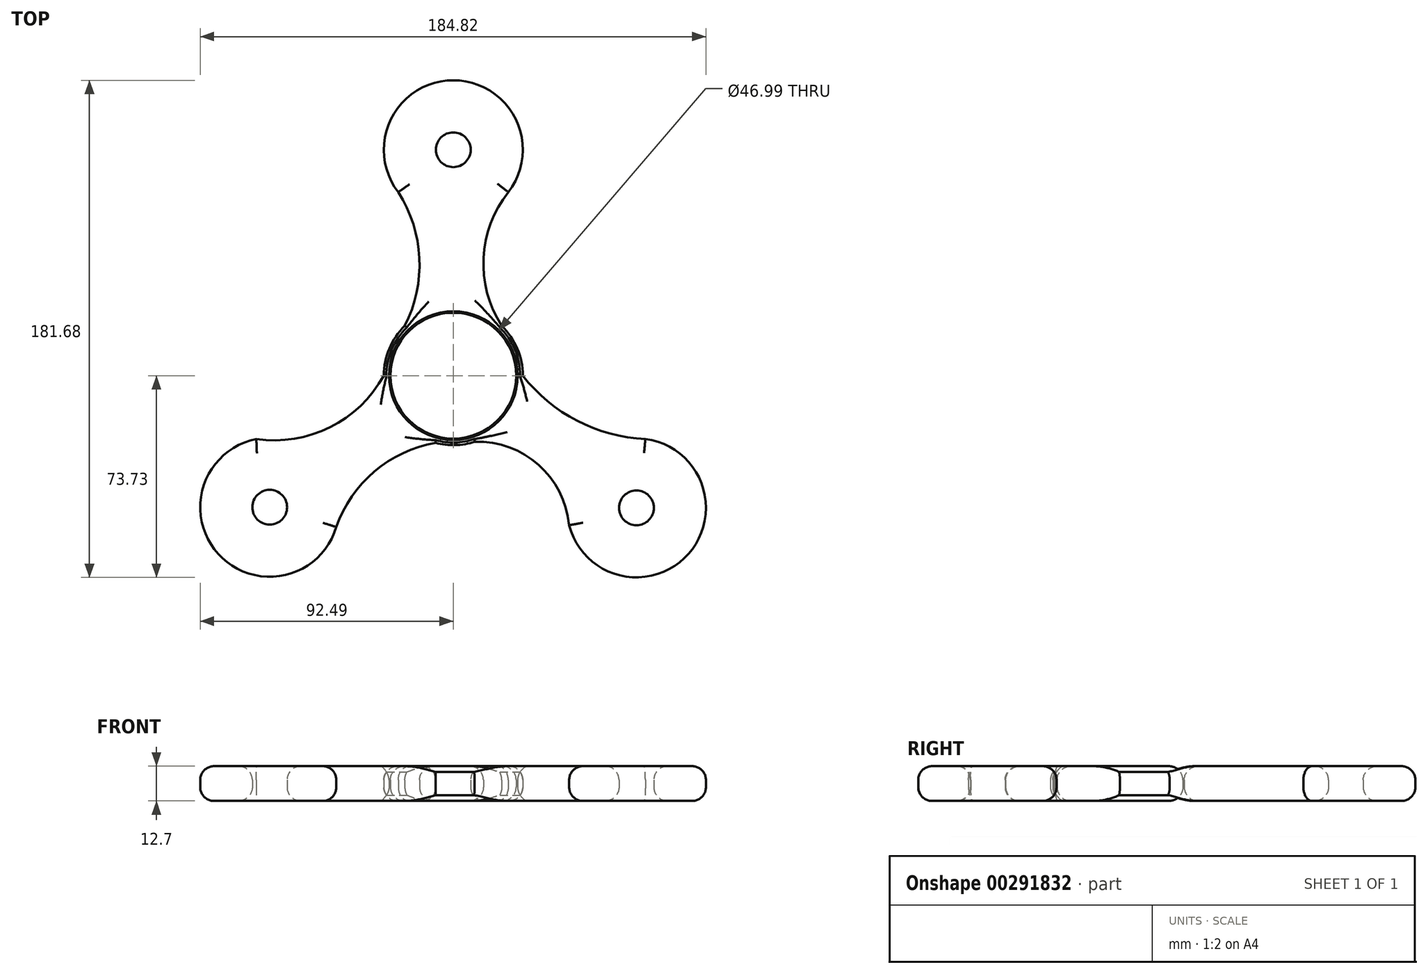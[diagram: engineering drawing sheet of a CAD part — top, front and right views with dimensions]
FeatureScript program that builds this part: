
annotation { "Feature Type Name" : "Feature", "Feature Type Description" : "" }
export const myFeature = defineFeature(function(context is Context, id is Id, definition is map)
    precondition{}
    {
        {
            var Q0;
            Q0=qCreatedBy(makeId("Top.planeOp"),FACE);
            var sketch = newSketch(context, id + "F0", { "sketchPlane" : qUnion([Q0])});
            skCircle(sketch, "E0", {"center": v(0, 0) * mm, "radius": 25.4 * mm});
            skCircle(sketch, "E1", {"center": v(0, 82.55) * mm, "radius": 25.4 * mm});
            skCircle(sketch, "E2", {"center": v(-67.09, -48.1) * mm, "radius": 25.4 * mm});
            skCircle(sketch, "E3", {"center": v(66.93, -48.33) * mm, "radius": 25.4 * mm});
            skArc(sketch, "E4", {"start": v(-71.96, -23.17) * mm, "mid": v(-45.05, -18.89) * mm, "end": v(-25.4, 0) * mm});
            skArc(sketch, "E5", {"start": v(-6.47, -24.56) * mm, "mid": v(-28.8, -35.02) * mm, "end": v(-42.74, -55.34) * mm});
            skArc(sketch, "E6", {"start": v(42.33, -54.66) * mm, "mid": v(31.12, -32.56) * mm, "end": v(7.8, -24.17) * mm});
            skArc(sketch, "E7", {"start": v(25.4, 0) * mm, "mid": v(45.25, -16.48) * mm, "end": v(70.19, -23.14) * mm});
            skArc(sketch, "E8", {"start": v(-17.72, 18.2) * mm, "mid": v(-12.4, 42.93) * mm, "end": v(-20.1, 67.03) * mm});
            skArc(sketch, "E9", {"start": v(20.1, 67.03) * mm, "mid": v(11.06, 43) * mm, "end": v(17.72, 18.2) * mm});
            skCircle(sketch, "E10", {"center": v(0, 82.55) * mm, "radius": 6.35 * mm});
            skCircle(sketch, "E11", {"center": v(-67.09, -48.1) * mm, "radius": 6.35 * mm});
            skCircle(sketch, "E12", {"center": v(66.93, -48.33) * mm, "radius": 6.35 * mm});
            skCircle(sketch, "E13", {"center": v(0, 0) * mm, "radius": 23.5 * mm});
            skSolve(sketch);
        }
        {
            var Q0;
            {var subQ0=sQuery(id+"F0.wireOp",EDGE,"E1");var subQ1=makeQuery(id+"F0.imprint","INTERSECT",VERTEX,{"derivedFrom":[subQ0,sQuery(id+"F0.wireOp",EDGE,"E8")]});Q0=makeQuery(id+"F0.imprint","IMPRINT",FACE,{"disambiguationData":[TD([[makeQuery(id+"F0.imprint","IMPRINT",EDGE,{"disambiguationData":[TD([[subQ1,-1.0]])],"derivedFrom":subQ0}),1.0]])]});}
            var Q1;
            {var subQ0=sQuery(id+"F0.wireOp",EDGE,"E8");Q1=makeQuery(id+"F0.imprint","IMPRINT",FACE,{"disambiguationData":[TD([[makeQuery(id+"F0.imprint","IMPRINT",EDGE,{"derivedFrom":subQ0}),-1.0]])]});}
            var Q2;
            {var subQ0=sQuery(id+"F0.wireOp",EDGE,"E0");var subQ5=makeQuery(id+"F0.imprint","INTERSECT",VERTEX,{"derivedFrom":[subQ0,sQuery(id+"F0.wireOp",EDGE,"E7")]});Q2=makeQuery(id+"F0.imprint","IMPRINT",FACE,{"disambiguationData":[TD([[makeQuery(id+"F0.imprint","IMPRINT",EDGE,{"disambiguationData":[TD([[subQ5,-1.0]])],"derivedFrom":subQ0}),1.0]])]});}
            var Q3;
            {var subQ3=sQuery(id+"F0.wireOp",EDGE,"E5");Q3=makeQuery(id+"F0.imprint","IMPRINT",FACE,{"disambiguationData":[TD([[makeQuery(id+"F0.imprint","IMPRINT",EDGE,{"derivedFrom":subQ3}),-1.0]])]});}
            var Q4;
            {var subQ0=sQuery(id+"F0.wireOp",EDGE,"E4");var subQ1=sQuery(id+"F0.wireOp",EDGE,"E2");var subQ2=makeQuery(id+"F0.imprint","INTERSECT",VERTEX,{"disambiguationData":[OD(0.0)],"derivedFrom":[subQ1,subQ0]});Q4=makeQuery(id+"F0.imprint","IMPRINT",FACE,{"disambiguationData":[TD([[makeQuery(id+"F0.imprint","IMPRINT",EDGE,{"disambiguationData":[TD([[subQ2,-1.0]])],"derivedFrom":subQ1}),1.0]])]});}
            var Q5;
            {var subQ0=sQuery(id+"F0.wireOp",EDGE,"E6");var subQ1=sQuery(id+"F0.wireOp",EDGE,"E0");var subQ2=makeQuery(id+"F0.imprint","INTERSECT",VERTEX,{"derivedFrom":[subQ1,subQ0]});Q5=makeQuery(id+"F0.imprint","IMPRINT",FACE,{"disambiguationData":[TD([[makeQuery(id+"F0.imprint","IMPRINT",EDGE,{"disambiguationData":[TD([[subQ2,-1.0]])],"derivedFrom":subQ1}),-1.0]])]});}
            var Q6;
            {var subQ0=sQuery(id+"F0.wireOp",EDGE,"E7");var subQ1=sQuery(id+"F0.wireOp",EDGE,"E3");var subQ2=makeQuery(id+"F0.imprint","INTERSECT",VERTEX,{"disambiguationData":[OD(1.0)],"derivedFrom":[subQ1,subQ0]});Q6=makeQuery(id+"F0.imprint","IMPRINT",FACE,{"disambiguationData":[TD([[makeQuery(id+"F0.imprint","IMPRINT",EDGE,{"disambiguationData":[TD([[subQ2,-1.0]])],"derivedFrom":subQ1}),1.0]])]});}
            var Q7;
            Q7=makeQuery(id+"F0.imprint","IMPRINT",FACE,{"disambiguationData":[TD([[makeQuery(id+"F0.imprint","IMPRINT",EDGE,{"derivedFrom":sQuery(id+"F0.wireOp",EDGE,"T1coXftw-NrjD-YKbX-frgJ-oNxXQp378vgS")}),1.0]])]});
            extrude(context, id + "F1", {"entities" : qUnion([Q0, Q1, Q2, Q3, Q4, Q5, Q6, Q7]), "depth" : 12.7 * mm, "offsetDistance" : 25.4 * mm});
        }
        {
            var Q0;
            {var subQ0=sQuery(id+"F0.wireOp",EDGE,"E0");Q0=makeQuery(id+"F1.opExtrude","CAP_EDGE",EDGE,{"disambiguationData":[OSD([subQ0]),TDD([makeQuery(id+"F0.imprint","IMPRINT",EDGE,{"disambiguationData":[TD([[makeQuery(id+"F0.imprint","INTERSECT",VERTEX,{"derivedFrom":[subQ0,sQuery(id+"F0.wireOp",EDGE,"E4")]}),1.0]])],"derivedFrom":subQ0})])],"isStart":false});}
            var Q1;
            {var subQ0=sQuery(id+"F0.wireOp",EDGE,"E0");Q1=makeQuery(id+"F1.opExtrude","CAP_EDGE",EDGE,{"disambiguationData":[OSD([subQ0]),TDD([makeQuery(id+"F0.imprint","IMPRINT",EDGE,{"disambiguationData":[TD([[makeQuery(id+"F0.imprint","INTERSECT",VERTEX,{"derivedFrom":[subQ0,sQuery(id+"F0.wireOp",EDGE,"E4")]}),1.0]])],"derivedFrom":subQ0})])],"isStart":true});}
            var Q2;
            Q2=makeQuery(id+"F1.opExtrude","CAP_EDGE",EDGE,{"disambiguationData":[OSD([sQuery(id+"F0.wireOp",EDGE,"E8")])],"isStart":true});
            var Q3;
            Q3=makeQuery(id+"F1.opExtrude","CAP_EDGE",EDGE,{"disambiguationData":[OSD([sQuery(id+"F0.wireOp",EDGE,"E8")])],"isStart":false});
            var Q4;
            Q4=makeQuery(id+"F1.opExtrude","CAP_EDGE",EDGE,{"disambiguationData":[OSD([sQuery(id+"F0.wireOp",EDGE,"E13")])],"isStart":false});
            var Q5;
            {var subQ0=sQuery(id+"F0.wireOp",EDGE,"E0");Q5=makeQuery(id+"F1.opExtrude","CAP_EDGE",EDGE,{"disambiguationData":[OSD([subQ0]),TDD([makeQuery(id+"F0.imprint","IMPRINT",EDGE,{"disambiguationData":[TD([[makeQuery(id+"F0.imprint","INTERSECT",VERTEX,{"derivedFrom":[subQ0,sQuery(id+"F0.wireOp",EDGE,"E7")]}),-1.0]])],"derivedFrom":subQ0})])],"isStart":false});}
            var Q6;
            {var subQ0=sQuery(id+"F0.wireOp",EDGE,"E0");Q6=makeQuery(id+"F1.opExtrude","CAP_EDGE",EDGE,{"disambiguationData":[OSD([subQ0]),TDD([makeQuery(id+"F0.imprint","IMPRINT",EDGE,{"disambiguationData":[TD([[makeQuery(id+"F0.imprint","INTERSECT",VERTEX,{"derivedFrom":[subQ0,sQuery(id+"F0.wireOp",EDGE,"E7")]}),-1.0]])],"derivedFrom":subQ0})])],"isStart":true});}
            var Q7;
            {var subQ0=sQuery(id+"F0.wireOp",EDGE,"E0");Q7=makeQuery(id+"F1.opExtrude","CAP_EDGE",EDGE,{"disambiguationData":[OSD([subQ0]),TDD([makeQuery(id+"F0.imprint","IMPRINT",EDGE,{"disambiguationData":[TD([[makeQuery(id+"F0.imprint","INTERSECT",VERTEX,{"derivedFrom":[subQ0,sQuery(id+"F0.wireOp",EDGE,"E5")]}),-1.0]])],"derivedFrom":subQ0})])],"isStart":true});}
            var Q8;
            Q8=makeQuery(id+"F1.opExtrude","CAP_EDGE",EDGE,{"disambiguationData":[OSD([sQuery(id+"F0.wireOp",EDGE,"E4")])],"isStart":true});
            var Q9;
            Q9=makeQuery(id+"F1.opExtrude","CAP_EDGE",EDGE,{"disambiguationData":[OSD([sQuery(id+"F0.wireOp",EDGE,"E5")])],"isStart":true});
            var Q10;
            Q10=makeQuery(id+"F1.opExtrude","CAP_EDGE",EDGE,{"disambiguationData":[OSD([sQuery(id+"F0.wireOp",EDGE,"E6")])],"isStart":true});
            var Q11;
            Q11=makeQuery(id+"F1.opExtrude","CAP_EDGE",EDGE,{"disambiguationData":[OSD([sQuery(id+"F0.wireOp",EDGE,"E6")])],"isStart":false});
            var Q12;
            Q12=makeQuery(id+"F1.opExtrude","CAP_EDGE",EDGE,{"disambiguationData":[OSD([sQuery(id+"F0.wireOp",EDGE,"E7")])],"isStart":true});
            var Q13;
            Q13=makeQuery(id+"F1.opExtrude","CAP_EDGE",EDGE,{"disambiguationData":[OSD([sQuery(id+"F0.wireOp",EDGE,"E7")])],"isStart":false});
            var Q14;
            Q14=makeQuery(id+"F1.opExtrude","CAP_EDGE",EDGE,{"disambiguationData":[OSD([sQuery(id+"F0.wireOp",EDGE,"E4")])],"isStart":false});
            var Q15;
            Q15=makeQuery(id+"F1.opExtrude","CAP_EDGE",EDGE,{"disambiguationData":[OSD([sQuery(id+"F0.wireOp",EDGE,"E5")])],"isStart":false});
            var Q16;
            Q16=makeQuery(id+"F1.opExtrude","CAP_EDGE",EDGE,{"disambiguationData":[OSD([sQuery(id+"F0.wireOp",EDGE,"E9")])],"isStart":false});
            var Q17;
            Q17=makeQuery(id+"F1.opExtrude","CAP_EDGE",EDGE,{"disambiguationData":[OSD([sQuery(id+"F0.wireOp",EDGE,"E3")])],"isStart":false});
            var Q18;
            Q18=makeQuery(id+"F1.opExtrude","CAP_EDGE",EDGE,{"disambiguationData":[OSD([sQuery(id+"F0.wireOp",EDGE,"E12")])],"isStart":false});
            var Q19;
            Q19=makeQuery(id+"F1.opExtrude","CAP_EDGE",EDGE,{"disambiguationData":[OSD([sQuery(id+"F0.wireOp",EDGE,"E12")])],"isStart":true});
            var Q20;
            Q20=makeQuery(id+"F1.opExtrude","CAP_EDGE",EDGE,{"disambiguationData":[OSD([sQuery(id+"F0.wireOp",EDGE,"E3")])],"isStart":true});
            var Q21;
            Q21=makeQuery(id+"F1.opExtrude","CAP_FACE",FACE,{"disambiguationData":[OSD([sQuery(id+"F0.wireOp",EDGE,"E0"),sQuery(id+"F0.wireOp",EDGE,"E1"),sQuery(id+"F0.wireOp",EDGE,"E2"),sQuery(id+"F0.wireOp",EDGE,"E3"),sQuery(id+"F0.wireOp",EDGE,"E4"),sQuery(id+"F0.wireOp",EDGE,"E5"),sQuery(id+"F0.wireOp",EDGE,"E6"),sQuery(id+"F0.wireOp",EDGE,"E7"),sQuery(id+"F0.wireOp",EDGE,"E8"),sQuery(id+"F0.wireOp",EDGE,"E9"),sQuery(id+"F0.wireOp",EDGE,"E10"),sQuery(id+"F0.wireOp",EDGE,"E11"),sQuery(id+"F0.wireOp",EDGE,"E12"),sQuery(id+"F0.wireOp",EDGE,"E13")])],"isStart":true});
            var Q22;
            Q22=makeQuery(id+"F1.opExtrude","CAP_FACE",FACE,{"disambiguationData":[OSD([sQuery(id+"F0.wireOp",EDGE,"E0"),sQuery(id+"F0.wireOp",EDGE,"E1"),sQuery(id+"F0.wireOp",EDGE,"E2"),sQuery(id+"F0.wireOp",EDGE,"E3"),sQuery(id+"F0.wireOp",EDGE,"E4"),sQuery(id+"F0.wireOp",EDGE,"E5"),sQuery(id+"F0.wireOp",EDGE,"E6"),sQuery(id+"F0.wireOp",EDGE,"E7"),sQuery(id+"F0.wireOp",EDGE,"E8"),sQuery(id+"F0.wireOp",EDGE,"E9"),sQuery(id+"F0.wireOp",EDGE,"E10"),sQuery(id+"F0.wireOp",EDGE,"E11"),sQuery(id+"F0.wireOp",EDGE,"E12"),sQuery(id+"F0.wireOp",EDGE,"E13")])],"isStart":false});
            var Q23;
            Q23=makeQuery(id+"F1.opExtrude","CAP_EDGE",EDGE,{"disambiguationData":[OSD([sQuery(id+"F0.wireOp",EDGE,"T1coXftw-NrjD-YKbX-frgJ-oNxXQp378vgS")])],"isStart":false});
            var Q24;
            Q24=makeQuery(id+"F1.opExtrude","CAP_EDGE",EDGE,{"disambiguationData":[OSD([sQuery(id+"F0.wireOp",EDGE,"E13")])],"isStart":true});
            fillet(context, id + "F2", {"entities" : qUnion([Q0, Q1, Q2, Q3, Q4, Q5, Q6, Q7, Q8, Q9, Q10, Q11, Q12, Q13, Q14, Q15, Q16, Q17, Q18, Q19, Q20, Q21, Q22, Q23, Q24]), "tangentPropagation" : true, "radius" : 5.08 * mm, "defaultsChanged" : false, "vertexSettings" : [], "allowEdgeOverflow" : false});
        }
        {
            var Q0;
            Q0=qCreatedBy(makeId("Top.planeOp"),FACE);
            var sketch = newSketch(context, id + "F3", { "sketchPlane" : qUnion([Q0])});
            skCircle(sketch, "E14", {"center": v(0, 0) * mm, "radius": 22.99 * mm});
            skSolve(sketch);
        }
        {
            var Q0;
            Q0=makeQuery(id+"F3.imprint","IMPRINT",FACE,{"disambiguationData":[TD([[makeQuery(id+"F3.imprint","IMPRINT",EDGE,{"derivedFrom":sQuery(id+"F3.wireOp",EDGE,"E14")}),1.0]])]});
            extrude(context, id + "F4", {"entities" : qUnion([Q0]), "depth" : 12.7 * mm, "offsetDistance" : 25.4 * mm});
        }
        {
            var Q0;
            Q0=makeQuery(id+"F4.opExtrude","CAP_EDGE",EDGE,{"disambiguationData":[OSD([sQuery(id+"F3.wireOp",EDGE,"E14")])],"isStart":false});
            var Q1;
            Q1=makeQuery(id+"F4.opExtrude","CAP_EDGE",EDGE,{"disambiguationData":[OSD([sQuery(id+"F3.wireOp",EDGE,"E14")])],"isStart":true});
            fillet(context, id + "F5", {"entities" : qUnion([Q0, Q1]), "tangentPropagation" : true, "radius" : 5.08 * mm, "defaultsChanged" : false, "vertexSettings" : [], "allowEdgeOverflow" : false});
        }
    });
